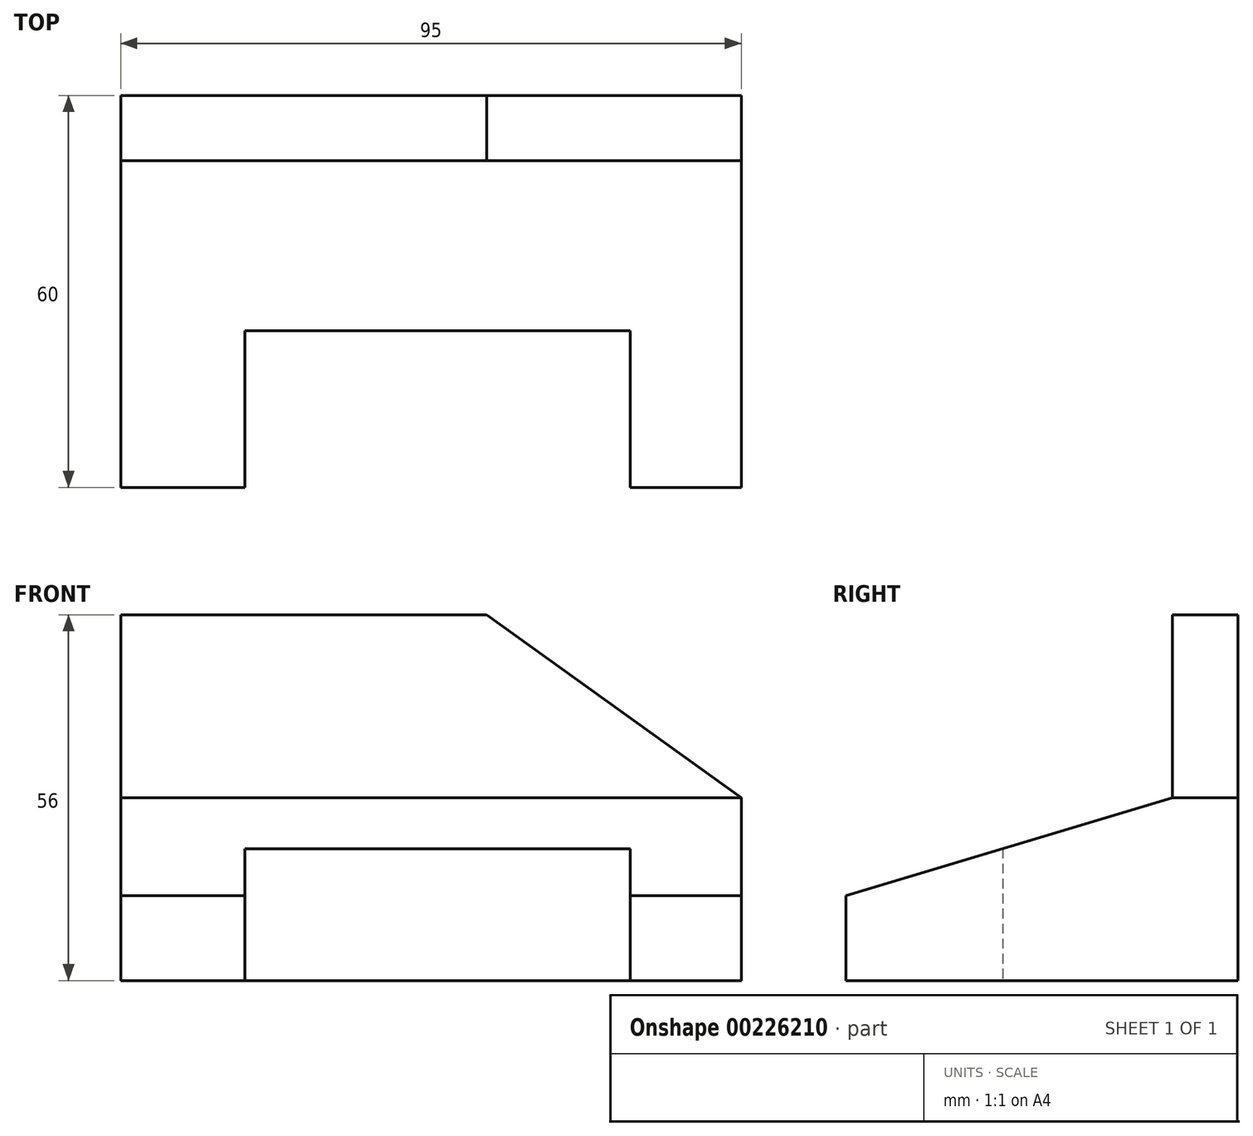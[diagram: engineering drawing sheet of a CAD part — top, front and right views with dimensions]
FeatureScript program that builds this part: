
annotation { "Feature Type Name" : "Feature", "Feature Type Description" : "" }
export const myFeature = defineFeature(function(context is Context, id is Id, definition is map)
    precondition{}
    {
        {
            var Q0;
            Q0=qCreatedBy(makeId("Right.planeOp"),FACE);
            var sketch = newSketch(context, id + "F0", { "sketchPlane" : qUnion([Q0])});
            skLineSegment(sketch, "E0", {"start": v(0, 0) * mm, "end": v(0, 56) * mm});
            skLineSegment(sketch, "E1", {"start": v(0, 56) * mm, "end": v(-10, 56) * mm});
            skLineSegment(sketch, "E2", {"start": v(-10, 56) * mm, "end": v(-10, 28) * mm});
            skLineSegment(sketch, "E3", {"start": v(-10, 28) * mm, "end": v(-60, 13) * mm});
            skLineSegment(sketch, "E4", {"start": v(-60, 13) * mm, "end": v(-60, 0) * mm});
            skLineSegment(sketch, "E5", {"start": v(-60, 0) * mm, "end": v(0, 0) * mm});
            skPoint(sketch, "E6", {"position": v(0, 28) * mm});
            skSolve(sketch);
        }
        {
            var Q0;
            Q0 = qSketchRegion(id + "F0", true);
            extrude(context, id + "F1", {"entities" : qUnion([Q0]), "depth" : 95 * mm});
        }
        {
            var Q0;
            Q0=makeQuery(id+"F1.opExtrude","SWEPT_FACE",FACE,{"disambiguationData":[OSD([sQuery(id+"F0.wireOp",EDGE,"E2")])]});
            var sketch = newSketch(context, id + "F2", { "sketchPlane" : qUnion([Q0])});
            skLineSegment(sketch, "E7", {"start": v(56, 56) * mm, "end": v(0, 56) * mm});
            skLineSegment(sketch, "E8", {"start": v(56, 56) * mm, "end": v(95, 28) * mm});
            skSolve(sketch);
        }
        {
            var Q0;
            {var subQ0=sQuery(id+"F2.wireOp",EDGE,"E8");Q0=makeQuery(id+"F2.imprint","IMPRINT",FACE,{"disambiguationData":[TD([[makeQuery(id+"F2.imprint","IMPRINT",EDGE,{"derivedFrom":subQ0}),1.0]])]});}
            extrude(context, id + "F3", {"entities" : qUnion([Q0]), "operationType" : NewBodyOperationType.REMOVE, "endBound" : BoundingType.THROUGH_ALL, "oppositeDirection" : true, "depth" : 25 * mm});
        }
        {
            var Q0;
            Q0=makeQuery(id+"F1.opExtrude","SWEPT_FACE",FACE,{"disambiguationData":[OSD([sQuery(id+"F0.wireOp",EDGE,"E5")])]});
            var sketch = newSketch(context, id + "F4", { "sketchPlane" : qUnion([Q0])});
            skLineSegment(sketch, "E9.bottom", {"start": v(19, 60) * mm, "end": v(78, 60) * mm});
            skLineSegment(sketch, "E9.top", {"start": v(19, 36) * mm, "end": v(78, 36) * mm});
            skLineSegment(sketch, "E9.left", {"start": v(19, 60) * mm, "end": v(19, 36) * mm});
            skLineSegment(sketch, "E9.right", {"start": v(78, 60) * mm, "end": v(78, 36) * mm});
            skSolve(sketch);
        }
        {
            var Q0;
            Q0 = qSketchRegion(id + "F4", true);
            var Q1;
            Q1=makeQuery(id+"F1.opExtrude","SWEPT_FACE",FACE,{"disambiguationData":[OSD([sQuery(id+"F0.wireOp",EDGE,"E3")])]});
            extrude(context, id + "F5", {"entities" : qUnion([Q0, Q1]), "operationType" : NewBodyOperationType.REMOVE, "endBound" : BoundingType.THROUGH_ALL, "oppositeDirection" : true, "depth" : 25 * mm});
        }
    });
